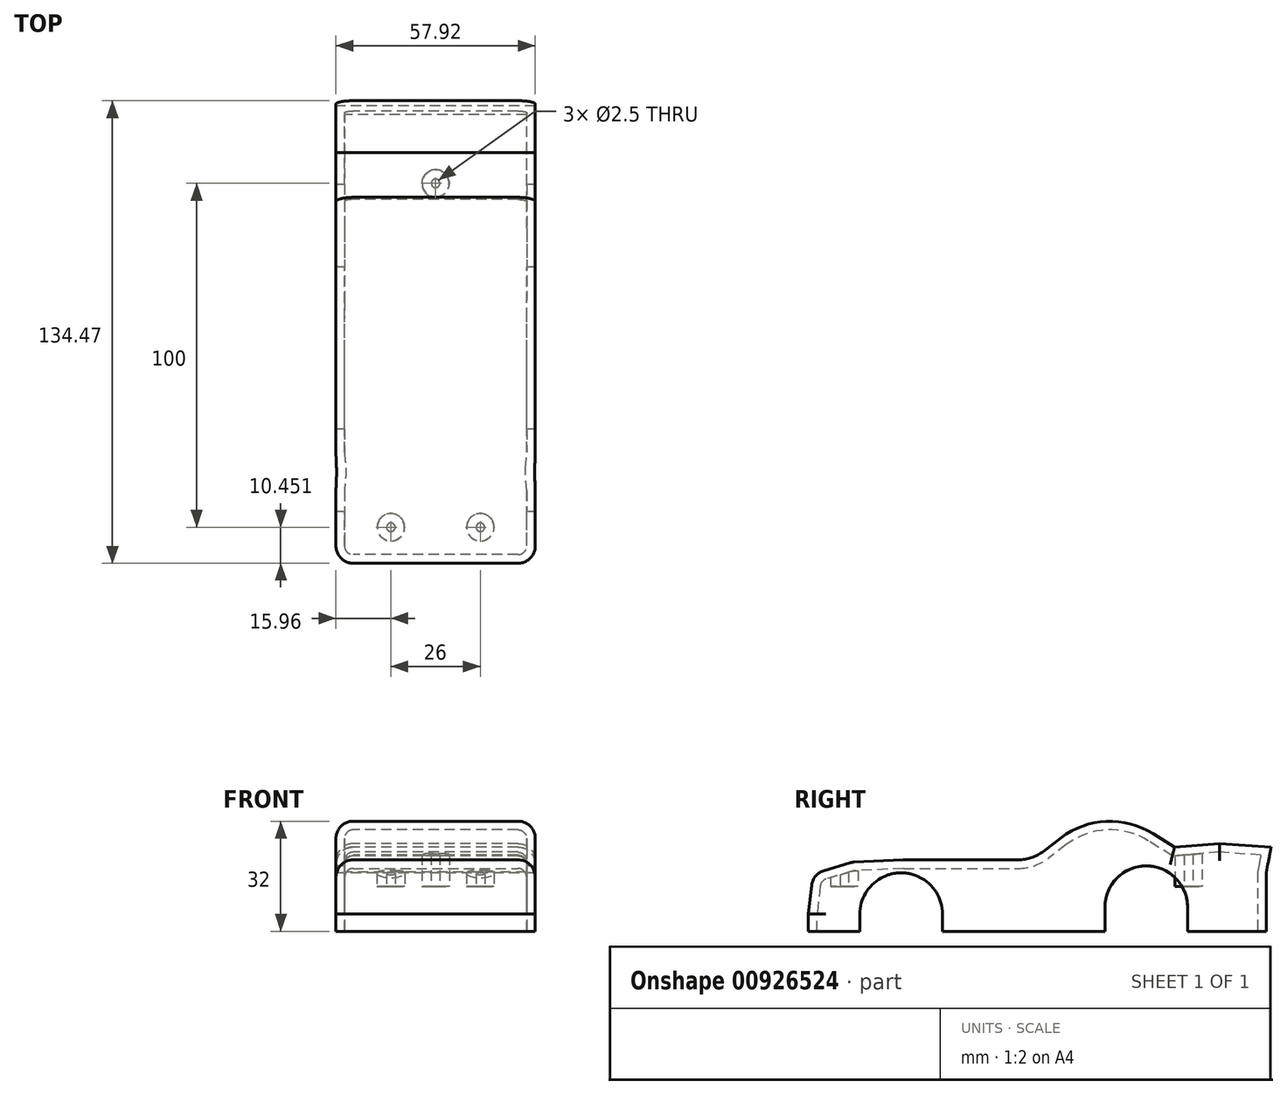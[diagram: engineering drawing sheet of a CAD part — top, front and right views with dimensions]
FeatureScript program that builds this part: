
annotation { "Feature Type Name" : "Feature", "Feature Type Description" : "" }
export const myFeature = defineFeature(function(context is Context, id is Id, definition is map)
    precondition{}
    {
        {
            var Q0;
            Q0=qCreatedBy(makeId("Top.planeOp"),FACE);
            cPlane(context, id + "F0", {"entities" : qUnion([Q0]), "cplaneType" : CPlaneType.OFFSET, "offset" : 8 * mm, "width" : 150 * mm, "height" : 150 * mm});
        }
        {
            var Q0;
            Q0=qCreatedBy(makeId("Right.planeOp"),FACE);
            var sketch = newSketch(context, id + "F1", { "sketchPlane" : qUnion([Q0])});
            skCircle(sketch, "E0", {"center": v(-19.78, 0) * mm, "radius": 12 * mm});
            skCircle(sketch, "E1", {"center": v(51.44, 2) * mm, "radius": 12 * mm});
            skLineSegment(sketch, "E2", {"start": v(-31.78, 0) * mm, "end": v(-46.73, 0) * mm});
            skLineSegment(sketch, "E3", {"start": v(-46.73, 0) * mm, "end": v(-45.78, 8.4) * mm});
            skLineSegment(sketch, "E4", {"start": v(-42.25, 12.63) * mm, "end": v(-34.65, 14.9) * mm});
            skLineSegment(sketch, "E5", {"start": v(-33.44, 15.1) * mm, "end": v(-19.1, 15.76) * mm});
            skLineSegment(sketch, "E6", {"start": v(-19.1, 15.76) * mm, "end": v(14.17, 15.76) * mm});
            skLineSegment(sketch, "E7", {"start": v(21.52, 18.24) * mm, "end": v(26.7, 22.19) * mm});
            skLineSegment(sketch, "E8", {"start": v(53.4, 23.42) * mm, "end": v(59.66, 19.5) * mm});
            skLineSegment(sketch, "E9", {"start": v(59.66, 19.5) * mm, "end": v(72.69, 20.52) * mm});
            skLineSegment(sketch, "E10", {"start": v(86.27, 11.94) * mm, "end": v(86.27, 0) * mm});
            skLineSegment(sketch, "E11", {"start": v(86.27, 0) * mm, "end": v(63.27, 0) * mm});
            skLineSegment(sketch, "E12", {"start": v(-7.78, 0) * mm, "end": v(39.6, 0) * mm});
            skPoint(sketch, "E13.visualSharp", {"position": v(-45.4, 11.68) * mm});
            skPoint(sketch, "E14.visualSharp", {"position": v(-34.06, 15.08) * mm});
            skArc(sketch, "E14.filletArc", {"start": v(-33.44, 15.1) * mm, "mid": v(-34.05, 15.04) * mm, "end": v(-34.65, 14.9) * mm});
            skPoint(sketch, "E15.visualSharp", {"position": v(-19.1, 15.76) * mm});
            skPoint(sketch, "E16.visualSharp", {"position": v(18.27, 15.76) * mm});
            skArc(sketch, "E16.filletArc", {"start": v(14.17, 15.76) * mm, "mid": v(18.05, 16.4) * mm, "end": v(21.52, 18.24) * mm});
            skPoint(sketch, "E17.visualSharp", {"position": v(39.62, 32.05) * mm});
            skArc(sketch, "E17.filletArc", {"start": v(53.4, 23.42) * mm, "mid": v(39.85, 26.97) * mm, "end": v(26.7, 22.19) * mm});
            skPoint(sketch, "E18.visualSharp", {"position": v(59.66, 19.5) * mm});
            skPoint(sketch, "E19.visualSharp", {"position": v(86.27, 21.57) * mm});
            skLineSegment(sketch, "E20", {"start": v(72.69, 20.52) * mm, "end": v(87.74, 19.46) * mm});
            skLineSegment(sketch, "E21", {"start": v(87.74, 19.46) * mm, "end": v(86.27, 11.94) * mm});
            skLineSegment(sketch, "E22", {"start": v(-31.78, 0) * mm, "end": v(-7.78, 0) * mm});
            skLineSegment(sketch, "E23", {"start": v(39.6, 0) * mm, "end": v(63.27, 0) * mm});
            skLineSegment(sketch, "E24", {"start": v(63.44, 2) * mm, "end": v(63.44, 0) * mm});
            skLineSegment(sketch, "E25", {"start": v(39.44, 2) * mm, "end": v(39.44, 0) * mm});
            skArc(sketch, "E26.filletArc", {"start": v(-42.25, 12.63) * mm, "mid": v(-44.65, 11.04) * mm, "end": v(-45.78, 8.4) * mm});
            skSolve(sketch);
        }
        {
            var Q0;
            Q0=qCreatedBy(id+"F0.planeOp",FACE);
            var sketch = newSketch(context, id + "F2", { "sketchPlane" : qUnion([Q0])});
            skLineSegment(sketch, "E27", {"start": v(0, -36.28) * mm, "end": v(0, 63.72) * mm, "construction": true});
            skLineSegment(sketch, "E28", {"start": v(0, -36.28) * mm, "end": v(13, -36.28) * mm, "construction": true});
            skLineSegment(sketch, "E29.MirrorCS", {"start": v(0, -36.28) * mm, "end": v(-13, -36.28) * mm, "construction": true});
            skCircle(sketch, "E30", {"center": v(13, -36.28) * mm, "radius": 4 * mm});
            skCircle(sketch, "E31", {"center": v(-13, -36.28) * mm, "radius": 4 * mm});
            skCircle(sketch, "E32", {"center": v(0, 63.72) * mm, "radius": 4 * mm});
            skCircle(sketch, "E33", {"center": v(-13, -36.28) * mm, "radius": 1.25 * mm});
            skCircle(sketch, "E34", {"center": v(13, -36.28) * mm, "radius": 1.25 * mm});
            skCircle(sketch, "E35", {"center": v(0, 63.72) * mm, "radius": 1.25 * mm});
            skSolve(sketch);
        }
        {
            var Q0;
            {var subQ1=sQuery(id+"F1.wireOp",EDGE,"E2");Q0=makeQuery(id+"F1.imprint","IMPRINT",FACE,{"disambiguationData":[TD([[makeQuery(id+"F1.imprint","IMPRINT",EDGE,{"derivedFrom":subQ1}),-1.0]])]});}
            var Q1;
            {var subQ0=sQuery(id+"F1.wireOp",EDGE,"E23");Q1=makeQuery(id+"F1.imprint","IMPRINT",FACE,{"disambiguationData":[TD([[makeQuery(id+"F1.imprint","IMPRINT",EDGE,{"derivedFrom":subQ0}),1.0]])]});}
            var Q2;
            {var subQ3=sQuery(id+"F1.wireOp",EDGE,"E25");Q2=makeQuery(id+"F1.imprint","IMPRINT",FACE,{"disambiguationData":[TD([[makeQuery(id+"F1.imprint","IMPRINT",EDGE,{"derivedFrom":subQ3}),1.0]])]});}
            var Q3;
            {var subQ3=sQuery(id+"F1.wireOp",EDGE,"E24");Q3=makeQuery(id+"F1.imprint","IMPRINT",FACE,{"disambiguationData":[TD([[makeQuery(id+"F1.imprint","IMPRINT",EDGE,{"derivedFrom":subQ3}),-1.0]])]});}
            var Q4;
            {var subQ0=sQuery(id+"F1.wireOp",EDGE,"E22");Q4=makeQuery(id+"F1.imprint","IMPRINT",FACE,{"disambiguationData":[TD([[makeQuery(id+"F1.imprint","IMPRINT",EDGE,{"derivedFrom":subQ0}),1.0]])]});}
            extrude(context, id + "F3", {"entities" : qUnion([Q0, Q1, Q2, Q3, Q4]), "depth" : 57.9 * mm, "symmetric" : true});
        }
        {
            var Q0;
            Q0=makeQuery(id+"F3.opExtrude","CAP_EDGE",EDGE,{"disambiguationData":[OSD([sQuery(id+"F1.wireOp",EDGE,"E3")])],"isStart":false});
            var Q1;
            Q1=makeQuery(id+"F3.opExtrude","CAP_EDGE",EDGE,{"disambiguationData":[OSD([sQuery(id+"F1.wireOp",EDGE,"E4")])],"isStart":false});
            var Q2;
            Q2=makeQuery(id+"F3.opExtrude","CAP_EDGE",EDGE,{"disambiguationData":[OSD([sQuery(id+"F1.wireOp",EDGE,"E6")])],"isStart":false});
            var Q3;
            Q3=makeQuery(id+"F3.opExtrude","CAP_EDGE",EDGE,{"disambiguationData":[OSD([sQuery(id+"F1.wireOp",EDGE,"E5")])],"isStart":false});
            var Q4;
            Q4=makeQuery(id+"F3.opExtrude","CAP_EDGE",EDGE,{"disambiguationData":[OSD([sQuery(id+"F1.wireOp",EDGE,"E14.filletArc")])],"isStart":false});
            var Q5;
            Q5=makeQuery(id+"F3.opExtrude","CAP_EDGE",EDGE,{"disambiguationData":[OSD([sQuery(id+"F1.wireOp",EDGE,"E9")])],"isStart":false});
            var Q6;
            Q6=makeQuery(id+"F3.opExtrude","CAP_EDGE",EDGE,{"disambiguationData":[OSD([sQuery(id+"F1.wireOp",EDGE,"E20")])],"isStart":false});
            var Q7;
            Q7=makeQuery(id+"F3.opExtrude","CAP_EDGE",EDGE,{"disambiguationData":[OSD([sQuery(id+"F1.wireOp",EDGE,"E20")])],"isStart":true});
            var Q8;
            Q8=makeQuery(id+"F3.opExtrude","CAP_EDGE",EDGE,{"disambiguationData":[OSD([sQuery(id+"F1.wireOp",EDGE,"E9")])],"isStart":true});
            var Q9;
            Q9=makeQuery(id+"F3.opExtrude","CAP_EDGE",EDGE,{"disambiguationData":[OSD([sQuery(id+"F1.wireOp",EDGE,"E8")])],"isStart":true});
            var Q10;
            Q10=makeQuery(id+"F3.opExtrude","CAP_EDGE",EDGE,{"disambiguationData":[OSD([sQuery(id+"F1.wireOp",EDGE,"E4")])],"isStart":true});
            var Q11;
            Q11=makeQuery(id+"F3.opExtrude","CAP_EDGE",EDGE,{"disambiguationData":[OSD([sQuery(id+"F1.wireOp",EDGE,"E26.filletArc")])],"isStart":false});
            var Q12;
            Q12=makeQuery(id+"F3.opExtrude","CAP_EDGE",EDGE,{"disambiguationData":[OSD([sQuery(id+"F1.wireOp",EDGE,"E26.filletArc")])],"isStart":true});
            var Q13;
            Q13=makeQuery(id+"F3.opExtrude","CAP_EDGE",EDGE,{"disambiguationData":[OSD([sQuery(id+"F1.wireOp",EDGE,"E3")])],"isStart":true});
            var Q14;
            Q14=makeQuery(id+"F3.opExtrude","CAP_EDGE",EDGE,{"disambiguationData":[OSD([sQuery(id+"F1.wireOp",EDGE,"E5")])],"isStart":true});
            var Q15;
            Q15=makeQuery(id+"F3.opExtrude","SWEPT_EDGE",EDGE,{"disambiguationData":[OSD([sQuery(id+"F1.wireOp",EDGE,"E5"),sQuery(id+"F1.wireOp",EDGE,"E6")])]});
            var Q16;
            Q16=makeQuery(id+"F3.opExtrude","SWEPT_EDGE",EDGE,{"disambiguationData":[OSD([sQuery(id+"F1.wireOp",EDGE,"E4"),sQuery(id+"F1.wireOp",EDGE,"E26.filletArc")])]});
            fillet(context, id + "F4", {"entities" : qUnion([Q0, Q1, Q2, Q3, Q4, Q5, Q6, Q7, Q8, Q9, Q10, Q11, Q12, Q13, Q14, Q15, Q16]), "radius" : 5 * mm, "tangentPropagation" : true, "allowEdgeOverflow" : false});
        }
        {
            var Q0;
            Q0=makeQuery(id+"F3.opExtrude","SWEPT_FACE",FACE,{"disambiguationData":[OSD([sQuery(id+"F1.wireOp",EDGE,"E2"),sQuery(id+"F1.wireOp",EDGE,"E11"),sQuery(id+"F1.wireOp",EDGE,"E12"),sQuery(id+"F1.wireOp",EDGE,"E22"),sQuery(id+"F1.wireOp",EDGE,"E23")])]});
            shell(context, id + "F5", {"entities" : qUnion([Q0]), "thickness" : 2.5 * mm});
        }
        {
            var Q0;
            {var subQ0=sQuery(id+"F1.wireOp",EDGE,"E22");Q0=makeQuery(id+"F1.imprint","IMPRINT",FACE,{"disambiguationData":[TD([[makeQuery(id+"F1.imprint","IMPRINT",EDGE,{"derivedFrom":subQ0}),1.0]])]});}
            var Q1;
            {var subQ0=sQuery(id+"F1.wireOp",EDGE,"E23");Q1=makeQuery(id+"F1.imprint","IMPRINT",FACE,{"disambiguationData":[TD([[makeQuery(id+"F1.imprint","IMPRINT",EDGE,{"derivedFrom":subQ0}),1.0]])]});}
            var Q2;
            {var subQ3=sQuery(id+"F1.wireOp",EDGE,"E25");Q2=makeQuery(id+"F1.imprint","IMPRINT",FACE,{"disambiguationData":[TD([[makeQuery(id+"F1.imprint","IMPRINT",EDGE,{"derivedFrom":subQ3}),1.0]])]});}
            var Q3;
            {var subQ3=sQuery(id+"F1.wireOp",EDGE,"E24");Q3=makeQuery(id+"F1.imprint","IMPRINT",FACE,{"disambiguationData":[TD([[makeQuery(id+"F1.imprint","IMPRINT",EDGE,{"derivedFrom":subQ3}),-1.0]])]});}
            extrude(context, id + "F6", {"entities" : qUnion([Q0, Q1, Q2, Q3]), "operationType" : NewBodyOperationType.REMOVE, "offsetDistance" : 25 * mm, "depth" : 60 * mm, "hasSecondDirection" : true, "secondDirectionBound" : BoundingType.THROUGH_ALL, "secondDirectionOppositeDirection" : true, "secondDirectionDepth" : 25 * mm, "symmetric" : true});
        }
        {
            var Q0;
            Q0=qSketchRegion(id+"F2",true);
            var Q1;
            Q1=makeQuery(id+"F3.opExtrude","SWEPT_BODY",BODY,{"disambiguationData":[OSD([sQuery(id+"F1.wireOp",EDGE,"E2"),sQuery(id+"F1.wireOp",EDGE,"E3"),sQuery(id+"F1.wireOp",EDGE,"E4"),sQuery(id+"F1.wireOp",EDGE,"E5"),sQuery(id+"F1.wireOp",EDGE,"E6"),sQuery(id+"F1.wireOp",EDGE,"E7"),sQuery(id+"F1.wireOp",EDGE,"E8"),sQuery(id+"F1.wireOp",EDGE,"E9"),sQuery(id+"F1.wireOp",EDGE,"E10"),sQuery(id+"F1.wireOp",EDGE,"E11"),sQuery(id+"F1.wireOp",EDGE,"E12"),sQuery(id+"F1.wireOp",EDGE,"E14.filletArc"),sQuery(id+"F1.wireOp",EDGE,"E16.filletArc"),sQuery(id+"F1.wireOp",EDGE,"E17.filletArc"),sQuery(id+"F1.wireOp",EDGE,"E20"),sQuery(id+"F1.wireOp",EDGE,"E21"),sQuery(id+"F1.wireOp",EDGE,"E22"),sQuery(id+"F1.wireOp",EDGE,"E23"),sQuery(id+"F1.wireOp",EDGE,"E26.filletArc")])]});
            extrude(context, id + "F7", {"entities" : qUnion([Q0]), "operationType" : NewBodyOperationType.ADD, "endBound" : BoundingType.UP_TO_BODY, "endBoundEntityBody" : qUnion([Q1]), "depth" : 25 * mm});
        }
        {
            var Q0;
            {var subQ0=sQuery(id+"F1.wireOp",EDGE,"E3");var subQ1=makeQuery(id+"F4.opFillet","BLEND_FACE",FACE,{"disambiguationData":[OSD([subQ0]),TDD([makeQuery(id+"F3.opExtrude","CAP_EDGE",EDGE,{"disambiguationData":[OSD([subQ0])],"isStart":false})])]});var subQ2=makeQuery(id+"F3.opExtrude","SWEPT_FACE",FACE,{"disambiguationData":[OSD([subQ0])]});var subQ3=sQuery(id+"F1.wireOp",EDGE,"E26.filletArc");var subQ4=sQuery(id+"F1.wireOp",EDGE,"E23");var subQ5=sQuery(id+"F1.wireOp",EDGE,"E22");var subQ6=sQuery(id+"F1.wireOp",EDGE,"E21");var subQ7=sQuery(id+"F1.wireOp",EDGE,"E20");var subQ8=sQuery(id+"F1.wireOp",EDGE,"E17.filletArc");var subQ9=sQuery(id+"F1.wireOp",EDGE,"E16.filletArc");var subQ10=sQuery(id+"F1.wireOp",EDGE,"E14.filletArc");var subQ11=sQuery(id+"F1.wireOp",EDGE,"E12");var subQ12=sQuery(id+"F1.wireOp",EDGE,"E11");var subQ13=sQuery(id+"F1.wireOp",EDGE,"E10");var subQ14=sQuery(id+"F1.wireOp",EDGE,"E9");var subQ15=sQuery(id+"F1.wireOp",EDGE,"E8");var subQ16=sQuery(id+"F1.wireOp",EDGE,"E7");var subQ17=sQuery(id+"F1.wireOp",EDGE,"E6");var subQ18=sQuery(id+"F1.wireOp",EDGE,"E5");var subQ19=sQuery(id+"F1.wireOp",EDGE,"E4");var subQ20=sQuery(id+"F1.wireOp",EDGE,"E2");var subQ21=makeQuery(id+"F3.opExtrude","CAP_FACE",FACE,{"disambiguationData":[OSD([subQ20,subQ0,subQ19,subQ18,subQ17,subQ16,subQ15,subQ14,subQ13,subQ12,subQ11,subQ10,subQ9,subQ8,subQ7,subQ6,subQ5,subQ4,subQ3])],"isStart":false});var subQ22=makeQuery(id+"F4.opFillet","BLEND_FACE",FACE,{"disambiguationData":[OSD([subQ0]),TDD([makeQuery(id+"F3.opExtrude","CAP_EDGE",EDGE,{"disambiguationData":[OSD([subQ0])],"isStart":true})])]});var subQ23=makeQuery(id+"F3.opExtrude","CAP_FACE",FACE,{"disambiguationData":[OSD([subQ20,subQ0,subQ19,subQ18,subQ17,subQ16,subQ15,subQ14,subQ13,subQ12,subQ11,subQ10,subQ9,subQ8,subQ7,subQ6,subQ5,subQ4,subQ3])],"isStart":true});Q0=makeQuery(id+"F6.boolean.opBoolean","SPLIT",FACE,{"disambiguationData":[TD([subQ23,subQ21,subQ2,subQ22,subQ1,makeQuery(id+"F5.opShell","OFFSET_FACE",FACE,{"disambiguationData":[OSD([subQ0]),TDD([subQ22])]}),makeQuery(id+"F5.opShell","OFFSET_FACE",FACE,{"disambiguationData":[OSD([subQ0]),TDD([subQ1])]}),makeQuery(id+"F5.opShell","OFFSET_FACE",FACE,{"disambiguationData":[OSD([subQ20,subQ0,subQ19,subQ18,subQ17,subQ16,subQ15,subQ14,subQ13,subQ12,subQ11,subQ10,subQ9,subQ8,subQ7,subQ6,subQ5,subQ4,subQ3]),TDD([subQ23])]}),makeQuery(id+"F5.opShell","OFFSET_FACE",FACE,{"disambiguationData":[OSD([subQ20,subQ0,subQ19,subQ18,subQ17,subQ16,subQ15,subQ14,subQ13,subQ12,subQ11,subQ10,subQ9,subQ8,subQ7,subQ6,subQ5,subQ4,subQ3]),TDD([subQ21])]}),makeQuery(id+"F5.opShell","OFFSET_FACE",FACE,{"disambiguationData":[OSD([subQ0]),TDD([subQ2])]}),makeQuery(id+"F6.opExtrude","SWEPT_FACE",FACE,{"disambiguationData":[OSD([sQuery(id+"F1.wireOp",EDGE,"E0")])]})])],"derivedFrom":makeQuery(id+"F3.opExtrude","SWEPT_FACE",FACE,{"disambiguationData":[OSD([subQ20,subQ12,subQ11,subQ5,subQ4])]})});}
            var Q1;
            {var subQ0=sQuery(id+"F1.wireOp",EDGE,"E26.filletArc");var subQ1=sQuery(id+"F1.wireOp",EDGE,"E23");var subQ2=sQuery(id+"F1.wireOp",EDGE,"E22");var subQ3=sQuery(id+"F1.wireOp",EDGE,"E21");var subQ4=sQuery(id+"F1.wireOp",EDGE,"E20");var subQ5=sQuery(id+"F1.wireOp",EDGE,"E17.filletArc");var subQ6=sQuery(id+"F1.wireOp",EDGE,"E16.filletArc");var subQ7=sQuery(id+"F1.wireOp",EDGE,"E14.filletArc");var subQ8=sQuery(id+"F1.wireOp",EDGE,"E12");var subQ9=sQuery(id+"F1.wireOp",EDGE,"E11");var subQ10=sQuery(id+"F1.wireOp",EDGE,"E10");var subQ11=sQuery(id+"F1.wireOp",EDGE,"E9");var subQ12=sQuery(id+"F1.wireOp",EDGE,"E8");var subQ13=sQuery(id+"F1.wireOp",EDGE,"E7");var subQ14=sQuery(id+"F1.wireOp",EDGE,"E6");var subQ15=sQuery(id+"F1.wireOp",EDGE,"E5");var subQ16=sQuery(id+"F1.wireOp",EDGE,"E4");var subQ17=sQuery(id+"F1.wireOp",EDGE,"E3");var subQ18=sQuery(id+"F1.wireOp",EDGE,"E2");var subQ19=makeQuery(id+"F3.opExtrude","CAP_FACE",FACE,{"disambiguationData":[OSD([subQ18,subQ17,subQ16,subQ15,subQ14,subQ13,subQ12,subQ11,subQ10,subQ9,subQ8,subQ7,subQ6,subQ5,subQ4,subQ3,subQ2,subQ1,subQ0])],"isStart":true});Q1=makeQuery(id+"F6.boolean.opBoolean","SPLIT",FACE,{"disambiguationData":[TD([subQ19,makeQuery(id+"F5.opShell","OFFSET_FACE",FACE,{"disambiguationData":[OSD([subQ18,subQ17,subQ16,subQ15,subQ14,subQ13,subQ12,subQ11,subQ10,subQ9,subQ8,subQ7,subQ6,subQ5,subQ4,subQ3,subQ2,subQ1,subQ0]),TDD([subQ19])]}),makeQuery(id+"F6.opExtrude","SWEPT_FACE",FACE,{"disambiguationData":[OSD([sQuery(id+"F1.wireOp",EDGE,"E0")])]}),makeQuery(id+"F6.opExtrude","SWEPT_FACE",FACE,{"disambiguationData":[OSD([sQuery(id+"F1.wireOp",EDGE,"E25")])]})])],"derivedFrom":makeQuery(id+"F3.opExtrude","SWEPT_FACE",FACE,{"disambiguationData":[OSD([subQ18,subQ9,subQ8,subQ2,subQ1])]})});}
            var Q2;
            {var subQ0=sQuery(id+"F1.wireOp",EDGE,"E26.filletArc");var subQ1=sQuery(id+"F1.wireOp",EDGE,"E23");var subQ2=sQuery(id+"F1.wireOp",EDGE,"E22");var subQ3=sQuery(id+"F1.wireOp",EDGE,"E21");var subQ4=sQuery(id+"F1.wireOp",EDGE,"E20");var subQ5=sQuery(id+"F1.wireOp",EDGE,"E17.filletArc");var subQ6=sQuery(id+"F1.wireOp",EDGE,"E16.filletArc");var subQ7=sQuery(id+"F1.wireOp",EDGE,"E14.filletArc");var subQ8=sQuery(id+"F1.wireOp",EDGE,"E12");var subQ9=sQuery(id+"F1.wireOp",EDGE,"E11");var subQ10=sQuery(id+"F1.wireOp",EDGE,"E10");var subQ11=sQuery(id+"F1.wireOp",EDGE,"E9");var subQ12=sQuery(id+"F1.wireOp",EDGE,"E8");var subQ13=sQuery(id+"F1.wireOp",EDGE,"E7");var subQ14=sQuery(id+"F1.wireOp",EDGE,"E6");var subQ15=sQuery(id+"F1.wireOp",EDGE,"E5");var subQ16=sQuery(id+"F1.wireOp",EDGE,"E4");var subQ17=sQuery(id+"F1.wireOp",EDGE,"E3");var subQ18=sQuery(id+"F1.wireOp",EDGE,"E2");var subQ19=makeQuery(id+"F3.opExtrude","CAP_FACE",FACE,{"disambiguationData":[OSD([subQ18,subQ17,subQ16,subQ15,subQ14,subQ13,subQ12,subQ11,subQ10,subQ9,subQ8,subQ7,subQ6,subQ5,subQ4,subQ3,subQ2,subQ1,subQ0])],"isStart":false});Q2=makeQuery(id+"F6.boolean.opBoolean","SPLIT",FACE,{"disambiguationData":[TD([subQ19,makeQuery(id+"F5.opShell","OFFSET_FACE",FACE,{"disambiguationData":[OSD([subQ18,subQ17,subQ16,subQ15,subQ14,subQ13,subQ12,subQ11,subQ10,subQ9,subQ8,subQ7,subQ6,subQ5,subQ4,subQ3,subQ2,subQ1,subQ0]),TDD([subQ19])]}),makeQuery(id+"F6.opExtrude","SWEPT_FACE",FACE,{"disambiguationData":[OSD([sQuery(id+"F1.wireOp",EDGE,"E0")])]}),makeQuery(id+"F6.opExtrude","SWEPT_FACE",FACE,{"disambiguationData":[OSD([sQuery(id+"F1.wireOp",EDGE,"E25")])]})])],"derivedFrom":makeQuery(id+"F3.opExtrude","SWEPT_FACE",FACE,{"disambiguationData":[OSD([subQ18,subQ9,subQ8,subQ2,subQ1])]})});}
            var Q3;
            {var subQ0=sQuery(id+"F1.wireOp",EDGE,"E10");var subQ1=sQuery(id+"F1.wireOp",EDGE,"E26.filletArc");var subQ2=sQuery(id+"F1.wireOp",EDGE,"E23");var subQ3=sQuery(id+"F1.wireOp",EDGE,"E22");var subQ4=sQuery(id+"F1.wireOp",EDGE,"E21");var subQ5=sQuery(id+"F1.wireOp",EDGE,"E20");var subQ6=sQuery(id+"F1.wireOp",EDGE,"E17.filletArc");var subQ7=sQuery(id+"F1.wireOp",EDGE,"E16.filletArc");var subQ8=sQuery(id+"F1.wireOp",EDGE,"E14.filletArc");var subQ9=sQuery(id+"F1.wireOp",EDGE,"E12");var subQ10=sQuery(id+"F1.wireOp",EDGE,"E11");var subQ11=sQuery(id+"F1.wireOp",EDGE,"E9");var subQ12=sQuery(id+"F1.wireOp",EDGE,"E8");var subQ13=sQuery(id+"F1.wireOp",EDGE,"E7");var subQ14=sQuery(id+"F1.wireOp",EDGE,"E6");var subQ15=sQuery(id+"F1.wireOp",EDGE,"E5");var subQ16=sQuery(id+"F1.wireOp",EDGE,"E4");var subQ17=sQuery(id+"F1.wireOp",EDGE,"E3");var subQ18=sQuery(id+"F1.wireOp",EDGE,"E2");var subQ19=makeQuery(id+"F3.opExtrude","CAP_FACE",FACE,{"disambiguationData":[OSD([subQ18,subQ17,subQ16,subQ15,subQ14,subQ13,subQ12,subQ11,subQ0,subQ10,subQ9,subQ8,subQ7,subQ6,subQ5,subQ4,subQ3,subQ2,subQ1])],"isStart":false});var subQ20=makeQuery(id+"F3.opExtrude","CAP_FACE",FACE,{"disambiguationData":[OSD([subQ18,subQ17,subQ16,subQ15,subQ14,subQ13,subQ12,subQ11,subQ0,subQ10,subQ9,subQ8,subQ7,subQ6,subQ5,subQ4,subQ3,subQ2,subQ1])],"isStart":true});Q3=makeQuery(id+"F6.boolean.opBoolean","SPLIT",FACE,{"disambiguationData":[TD([subQ20,subQ19,makeQuery(id+"F3.opExtrude","SWEPT_FACE",FACE,{"disambiguationData":[OSD([subQ0])]}),makeQuery(id+"F5.opShell","OFFSET_FACE",FACE,{"disambiguationData":[OSD([subQ0])]}),makeQuery(id+"F5.opShell","OFFSET_FACE",FACE,{"disambiguationData":[OSD([subQ18,subQ17,subQ16,subQ15,subQ14,subQ13,subQ12,subQ11,subQ0,subQ10,subQ9,subQ8,subQ7,subQ6,subQ5,subQ4,subQ3,subQ2,subQ1]),TDD([subQ20])]}),makeQuery(id+"F5.opShell","OFFSET_FACE",FACE,{"disambiguationData":[OSD([subQ18,subQ17,subQ16,subQ15,subQ14,subQ13,subQ12,subQ11,subQ0,subQ10,subQ9,subQ8,subQ7,subQ6,subQ5,subQ4,subQ3,subQ2,subQ1]),TDD([subQ19])]}),makeQuery(id+"F6.opExtrude","SWEPT_FACE",FACE,{"disambiguationData":[OSD([sQuery(id+"F1.wireOp",EDGE,"E24")])]})])],"derivedFrom":makeQuery(id+"F3.opExtrude","SWEPT_FACE",FACE,{"disambiguationData":[OSD([subQ18,subQ10,subQ9,subQ3,subQ2])]})});}
            extrude(context, id + "F8", {"entities" : qUnion([Q0, Q1, Q2, Q3]), "operationType" : NewBodyOperationType.ADD, "depth" : 5 * mm});
        }
    });
